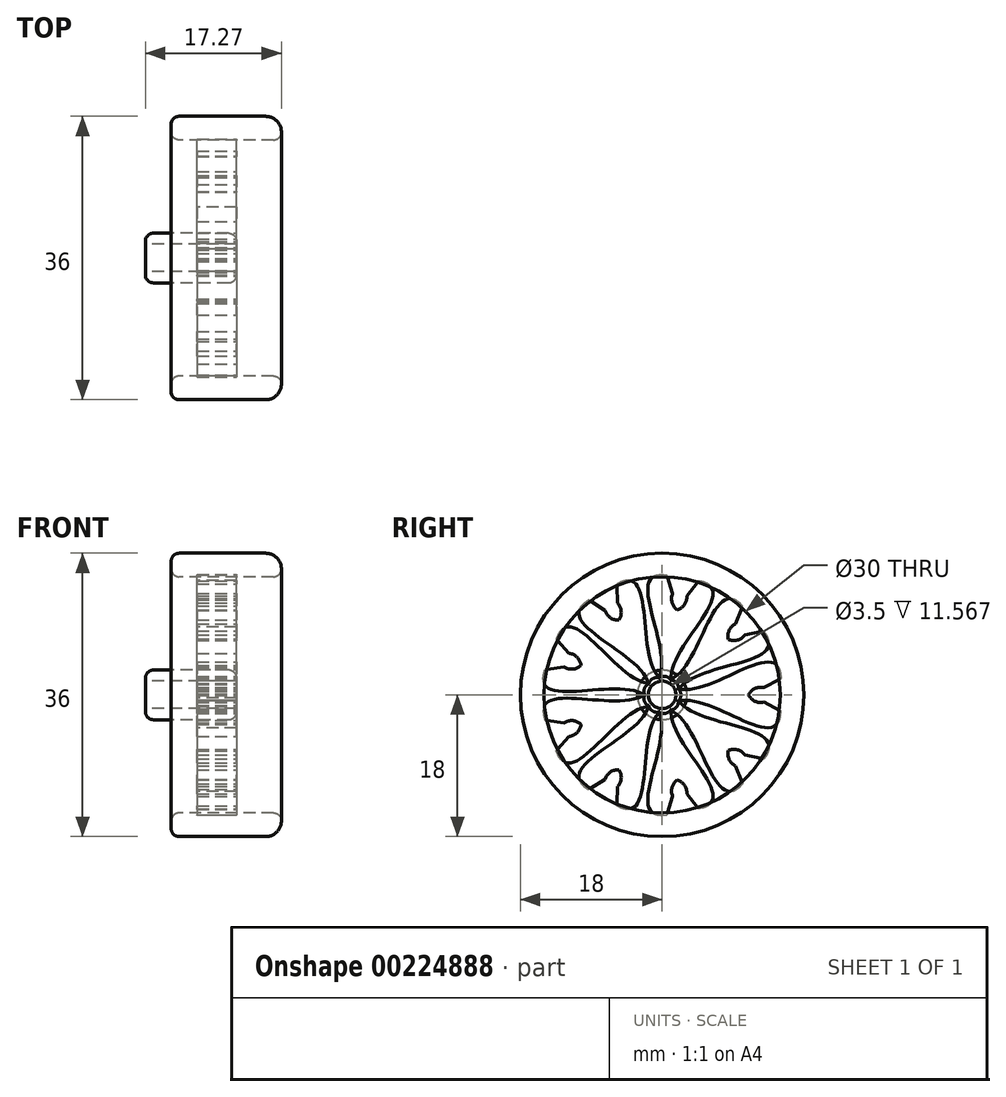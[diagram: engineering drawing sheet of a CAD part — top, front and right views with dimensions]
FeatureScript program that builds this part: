
annotation { "Feature Type Name" : "Feature", "Feature Type Description" : "" }
export const myFeature = defineFeature(function(context is Context, id is Id, definition is map)
    precondition{}
    {
        {
            var Q0;
            Q0=qCreatedBy(makeId("Top.planeOp"),FACE);
            var sketch = newSketch(context, id + "F0", { "sketchPlane" : qUnion([Q0])});
            skLineSegment(sketch, "E0", {"start": v(0, 16) * mm, "end": v(0, 17) * mm});
            skLineSegment(sketch, "E1", {"start": v(1, 18) * mm, "end": v(12, 18) * mm});
            skLineSegment(sketch, "E2", {"start": v(14, 16) * mm, "end": v(14, 16) * mm});
            skLineSegment(sketch, "E3", {"start": v(13, 15) * mm, "end": v(1, 15) * mm});
            skLineSegment(sketch, "E4", {"start": v(-50.22, 0) * mm, "end": v(7.2, 0) * mm, "construction": true});
            skPoint(sketch, "E5.visualSharp", {"position": v(14, 18) * mm});
            skArc(sketch, "E5.filletArc", {"start": v(14, 16) * mm, "mid": v(13.41, 17.41) * mm, "end": v(12, 18) * mm});
            skPoint(sketch, "E6.visualSharp", {"position": v(14, 15) * mm});
            skArc(sketch, "E6.filletArc", {"start": v(13, 15) * mm, "mid": v(13.7, 15.3) * mm, "end": v(14, 16) * mm});
            skPoint(sketch, "E7.visualSharp", {"position": v(0, 18) * mm});
            skArc(sketch, "E7.filletArc", {"start": v(1, 18) * mm, "mid": v(0.3, 17.7) * mm, "end": v(0, 17) * mm});
            skPoint(sketch, "E8.newPointA", {"position": v(0, 0) * mm});
            skArc(sketch, "E8.filletArc", {"start": v(0, 16) * mm, "mid": v(0.3, 15.3) * mm, "end": v(1, 15) * mm});
            skPoint(sketch, "E9.visualSharp", {"position": v(0, 2.85) * mm});
            skLineSegment(sketch, "E10", {"start": v(2, 3.15) * mm, "end": v(-2.27, 3.15) * mm});
            skLineSegment(sketch, "E11", {"start": v(-3.27, 0) * mm, "end": v(0, 0) * mm});
            skLineSegment(sketch, "E12", {"start": v(0, 0) * mm, "end": v(6.43, 0) * mm});
            skLineSegment(sketch, "E13", {"start": v(7.3, 3.15) * mm, "end": v(2, 3.15) * mm});
            skLineSegment(sketch, "E14", {"start": v(-3.27, 1.75) * mm, "end": v(8.3, 1.75) * mm});
            skLineSegment(sketch, "E15", {"start": v(-3.27, 1.75) * mm, "end": v(-3.27, 2.15) * mm});
            skLineSegment(sketch, "E16", {"start": v(8.3, 1.75) * mm, "end": v(8.3, 2.15) * mm});
            skPoint(sketch, "E17.visualSharp", {"position": v(8.3, 3.15) * mm});
            skArc(sketch, "E17.filletArc", {"start": v(8.3, 2.15) * mm, "mid": v(8, 2.86) * mm, "end": v(7.3, 3.15) * mm});
            skPoint(sketch, "E18.visualSharp", {"position": v(-3.27, 3.15) * mm});
            skArc(sketch, "E18.filletArc", {"start": v(-2.27, 3.15) * mm, "mid": v(-2.98, 2.86) * mm, "end": v(-3.27, 2.15) * mm});
            skSolve(sketch);
        }
        {
            var Q0;
            Q0=qSketchRegion(id+"F0",true);
            var Q1;
            Q1=sQuery(id+"F0.wireOp",EDGE,"E4");
            revolve(context, id + "F1", {"entities" : qUnion([Q0]), "axis" : qUnion([Q1]), "revolveType" : RevolveType.FULL});
        }
        {
            var Q0;
            Q0=makeQuery(id+"F1.opRevolve","SWEPT_FACE",FACE,{"disambiguationData":[OSD([sQuery(id+"F0.wireOp",EDGE,"E16")])]});
            var sketch = newSketch(context, id + "F2", { "sketchPlane" : qUnion([Q0])});
            skArc(sketch, "E19", {"start": v(15.09, -2.06) * mm, "mid": v(15.68, 0) * mm, "end": v(15.09, 2.06) * mm});
            skArc(sketch, "E20", {"start": v(1.99, -0.83) * mm, "mid": v(2.39, 0) * mm, "end": v(1.99, 0.83) * mm});
            skFitSpline(sketch, "E21", {"points": [v(1.99, 0.83) * mm, v(15.09, 2.06) * mm], "startDerivative": vector(12.6, -3.99) * mm, "endDerivative": vector(0.27, -17.74) * mm});
            skArc(sketch, "E22", {"start": v(12.92, 0.92) * mm, "mid": v(11.79, 0.8) * mm, "end": v(10.98, 0) * mm});
            skArc(sketch, "E23.MirrorCS", {"start": v(12.92, -0.92) * mm, "mid": v(11.79, -0.8) * mm, "end": v(10.98, 0) * mm});
            skFitSpline(sketch, "E24.MirrorCS", {"points": [v(1.99, -0.83) * mm, v(15.09, -2.06) * mm], "startDerivative": vector(12.6, 3.99) * mm, "endDerivative": vector(0.27, 17.74) * mm});
            skLineSegment(sketch, "E25", {"start": v(12.92, 0.92) * mm, "end": v(15.09, 2.06) * mm});
            skLineSegment(sketch, "E26", {"start": v(12.92, -0.92) * mm, "end": v(15.09, -2.06) * mm});
            skSolve(sketch);
        }
        {
            var Q0;
            Q0=makeQuery(id+"F2.imprint","IMPRINT",FACE,{"disambiguationData":[TD([[makeQuery(id+"F2.imprint","IMPRINT",EDGE,{"derivedFrom":sQuery(id+"F2.wireOp",EDGE,"E20")}),-1.0]])]});
            extrude(context, id + "F3", {"entities" : qUnion([Q0]), "oppositeDirection" : true, "depth" : 5 * mm});
        }
        {
            var Q0;
            Q0=makeQuery(id+"F3.opExtrude","SWEPT_BODY",BODY,{"disambiguationData":[OSD([sQuery(id+"F2.wireOp",EDGE,"E20"),sQuery(id+"F2.wireOp",EDGE,"E21"),sQuery(id+"F2.wireOp",EDGE,"E22"),sQuery(id+"F2.wireOp",EDGE,"E23.MirrorCS"),sQuery(id+"F2.wireOp",EDGE,"E24.MirrorCS"),sQuery(id+"F2.wireOp",EDGE,"E25"),sQuery(id+"F2.wireOp",EDGE,"E26")])]});
            var Q1;
            Q1=makeQuery(id+"F1.opRevolve","SWEPT_EDGE",EDGE,{"disambiguationData":[OSD([sQuery(id+"F0.wireOp",EDGE,"E5.filletArc"),sQuery(id+"F0.wireOp",EDGE,"E6.filletArc")])]});
            circularPattern(context, id + "F4", {"entities" : qUnion([Q0]), "axis" : qUnion([Q1]), "angle" : 360 * degree, "instanceCount" : 9, "equalSpace" : true});
        }
    });
